# Revit family: ПИК ЭНЕРГО WP Боковой поддерживающий зажим, консольный WPHS
name_source: partatom
category: Обобщенные модели
revit_build: Autodesk Revit 2015 (Build: 20141119_1515(x64)
units: mm (PartAtom-declared; Revit-internal decimal feet)

## types (9) — shared parameters
Отметка по умолчанию = 1219 мм
Рзм.B = 40 мм
Рзм.H = 40 мм
Рзм.L = 200 мм
Рзм.t = 3 мм
Спец.URLСсылкаКрепленияЛоткаКабельногоКанала = http://www.pik-energo.ru
Спец.ЕдИзмКрепленияЛоткаКабельногоКанала = шт.
Спец.ИзготовительКрепленияЛоткаКабельногоКанала = ПИК-ЭНЕРГО

## per-type parameters (varying)
| type | Пр.НаименованиеКрепленияЛоткаКабельногоКанала | Спец.КодОборудИзделияМатериалаКрепленияЛоткаКабельногоКанала | Спец.МассаКрепленияЛоткаКабельногоКанала | Спец.НаименованиеИТенхХарКрепленияЛоткаКабельногоКанала |
| WPHS-K S | Боковой поддерживающий зажим, консольный, сталь оцинкованная методом Сендзимира, по DIN EN 10346 | WPHS-K S | 0.51 kg | Боковой поддерживающий зажим, консольный |
| WPHS-K F | Боковой поддерживающий зажим, консольный, сталь горячеоцинкованная, по DIN EN ISO 1461 | WPHS-K S | 0.55 kg | Боковой поддерживающий зажим, консольный |
| WPHS-K E | Боковой поддерживающий зажим, консольный, ержавеющая сталь (1.4301 (V 2A)) | WPHS-K S | 0.51 kg | Боковой поддерживающий зажим, консольный |
| WPHS-P E | Боковой поддерживающий зажим, балочный, нержавеющая сталь (1.4301 (V 2A)) | WPHS-P S | 0.54 kg | Боковой поддерживающий зажим, балочный |
| WPHS-P F | Боковой поддерживающий зажим, балочный, сталь горячеоцинкованная, по DIN EN ISO 1461 | WPHS-P S | 0.58 kg | Боковой поддерживающий зажим, балочный |
| WPHS-P S | Боковой поддерживающий зажим, балочный, сталь оцинкованная методом Сендзимира, по DIN EN 10346 | WPHS-P S | 0.54 kg | Боковой поддерживающий зажим, балочный |
| WPHS-A S | Боковой поддерживающий зажим, канальный, сталь оцинкованная методом Сендзимира, по DIN EN 10346 | WPHS-A S | 0.53 kg | Боковой поддерживающий зажим, канальный |
| WPHS-A F | Боковой поддерживающий зажим, канальный, сталь горячеоцинкованная, по DIN EN ISO 1461 | WPHS-A S | 0.57 kg | Боковой поддерживающий зажим, канальный |
| WPHS-A E | Боковой поддерживающий зажим, канальный, нержавеющая сталь (1.4301 (V 2A)) | WPHS-A S | 0.53 kg | Боковой поддерживающий зажим, консольный |

## geometry (parser evidence)
native form markers: Blend x2
no freeform markers — native parametric forms only
